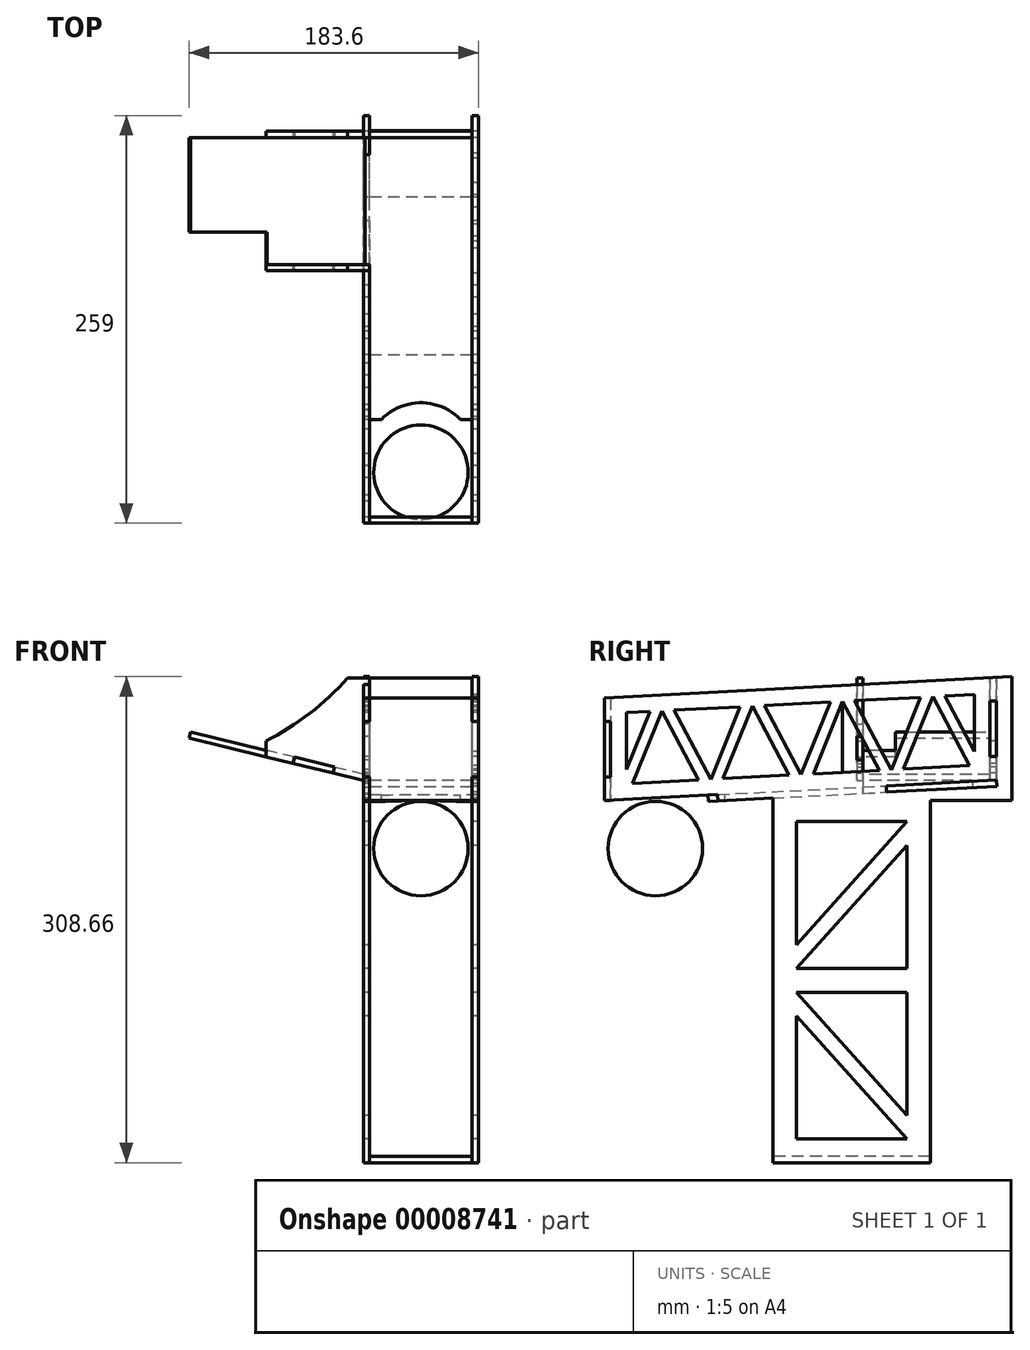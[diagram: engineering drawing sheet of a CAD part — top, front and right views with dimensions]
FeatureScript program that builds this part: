
annotation { "Feature Type Name" : "Feature", "Feature Type Description" : "" }
export const myFeature = defineFeature(function(context is Context, id is Id, definition is map)
    precondition{}
    {
        {
            var Q0;
            Q0=qCreatedBy(makeId("Right.planeOp"),FACE);
            var sketch = newSketch(context, id + "F0", { "sketchPlane" : qUnion([Q0])});
            skLineSegment(sketch, "E0", {"start": v(0, 0) * mm, "end": v(71.9, 3.77) * mm});
            skLineSegment(sketch, "E1", {"start": v(249, 78.14) * mm, "end": v(0, 65.09) * mm});
            skLineSegment(sketch, "E2", {"start": v(0, 65.09) * mm, "end": v(0, 50.09) * mm});
            skLineSegment(sketch, "E3.top", {"start": v(71.9, 0) * mm, "end": v(0, 0) * mm, "construction": true});
            skPoint(sketch, "E4.orphan", {"position": v(249, 13.05) * mm});
            skLineSegment(sketch, "E5", {"start": v(249, 13.05) * mm, "end": v(249.2, 9.06) * mm, "construction": true});
            skLineSegment(sketch, "E6", {"start": v(249, 78.14) * mm, "end": v(249, 13.05) * mm, "construction": true});
            skLineSegment(sketch, "E7", {"start": v(249.2, 9.06) * mm, "end": v(249, 13.05) * mm});
            skLineSegment(sketch, "E8", {"start": v(179.1, 9.39) * mm, "end": v(179.3, 5.4) * mm});
            skLineSegment(sketch, "E9", {"start": v(179.3, 5.4) * mm, "end": v(249.2, 9.06) * mm});
            skLineSegment(sketch, "E10.bottom", {"start": v(249, 63.14) * mm, "end": v(245, 63.14) * mm});
            skLineSegment(sketch, "E10.top", {"start": v(249, 28.14) * mm, "end": v(245, 28.14) * mm});
            skLineSegment(sketch, "E10.left", {"start": v(249, 63.14) * mm, "end": v(249, 28.14) * mm});
            skLineSegment(sketch, "E10.right", {"start": v(245, 63.14) * mm, "end": v(245, 28.14) * mm});
            skLineSegment(sketch, "E11", {"start": v(179.1, 9.39) * mm, "end": v(249, 13.05) * mm});
            skLineSegment(sketch, "E12", {"start": v(72.11, -0.23) * mm, "end": v(107.06, 1.6) * mm});
            skLineSegment(sketch, "E13", {"start": v(71.9, 3.77) * mm, "end": v(72.11, -0.23) * mm});
            skLineSegment(sketch, "E14.bottom", {"start": v(0, 50.09) * mm, "end": v(4, 50.09) * mm});
            skLineSegment(sketch, "E14.top", {"start": v(0, 15.09) * mm, "end": v(4, 15.09) * mm});
            skLineSegment(sketch, "E14.right", {"start": v(4, 50.09) * mm, "end": v(4, 15.09) * mm});
            skLineSegment(sketch, "E15.trimOffspring", {"start": v(0, 15.09) * mm, "end": v(0, 0) * mm});
            skLineSegment(sketch, "E16", {"start": v(14, 55.8) * mm, "end": v(28.9, 56.59) * mm});
            skLineSegment(sketch, "E17", {"start": v(235, 67.4) * mm, "end": v(235, 31.3) * mm});
            skLineSegment(sketch, "E18", {"start": v(231.93, 22.17) * mm, "end": v(190.02, 19.97) * mm});
            skLineSegment(sketch, "E19", {"start": v(14, 19.72) * mm, "end": v(14, 55.8) * mm});
            skLineSegment(sketch, "E20", {"start": v(44.32, 57.4) * mm, "end": v(67.63, 13.56) * mm});
            skLineSegment(sketch, "E21", {"start": v(75.35, 13.96) * mm, "end": v(93.95, 60) * mm});
            skLineSegment(sketch, "E22", {"start": v(101.66, 60.4) * mm, "end": v(124.97, 16.56) * mm});
            skLineSegment(sketch, "E23", {"start": v(132.68, 16.97) * mm, "end": v(151.28, 63) * mm});
            skLineSegment(sketch, "E24", {"start": v(159, 63.4) * mm, "end": v(182.3, 19.57) * mm});
            skLineSegment(sketch, "E25", {"start": v(36.6, 57) * mm, "end": v(59.92, 13.15) * mm});
            skLineSegment(sketch, "E26", {"start": v(67.63, 13.56) * mm, "end": v(86.23, 59.6) * mm});
            skLineSegment(sketch, "E27", {"start": v(93.95, 60) * mm, "end": v(117.26, 16.16) * mm});
            skLineSegment(sketch, "E28", {"start": v(124.97, 16.56) * mm, "end": v(143.57, 62.6) * mm});
            skLineSegment(sketch, "E29", {"start": v(151.28, 63) * mm, "end": v(174.6, 19.16) * mm});
            skLineSegment(sketch, "E30", {"start": v(182.3, 19.57) * mm, "end": v(200.9, 65.6) * mm});
            skLineSegment(sketch, "E31", {"start": v(190.02, 19.97) * mm, "end": v(208.62, 66) * mm});
            skLineSegment(sketch, "E32", {"start": v(208.62, 66) * mm, "end": v(231.93, 22.17) * mm});
            skLineSegment(sketch, "E33", {"start": v(216.33, 66.41) * mm, "end": v(235, 31.3) * mm});
            skLineSegment(sketch, "E34", {"start": v(36.6, 57) * mm, "end": v(18, 10.96) * mm});
            skLineSegment(sketch, "E35", {"start": v(28.9, 56.59) * mm, "end": v(14, 19.72) * mm});
            skLineSegment(sketch, "E36.trimOffspring", {"start": v(44.32, 57.4) * mm, "end": v(86.23, 59.6) * mm});
            skLineSegment(sketch, "E37.trimOffspring", {"start": v(59.92, 13.15) * mm, "end": v(18, 10.96) * mm});
            skLineSegment(sketch, "E38.trimOffspring", {"start": v(101.66, 60.4) * mm, "end": v(143.57, 62.6) * mm});
            skLineSegment(sketch, "E39.trimOffspring", {"start": v(159, 63.4) * mm, "end": v(200.9, 65.6) * mm});
            skLineSegment(sketch, "E40.trimOffspring", {"start": v(117.26, 16.16) * mm, "end": v(75.35, 13.96) * mm});
            skLineSegment(sketch, "E41.trimOffspring", {"start": v(216.33, 66.41) * mm, "end": v(235, 67.4) * mm});
            skLineSegment(sketch, "E42", {"start": v(132.68, 16.97) * mm, "end": v(174.6, 19.16) * mm});
            skLineSegment(sketch, "E43", {"start": v(107.06, 1.6) * mm, "end": v(107.06, -230) * mm});
            skLineSegment(sketch, "E44", {"start": v(107.06, -230) * mm, "end": v(207.06, -230) * mm});
            skLineSegment(sketch, "E45", {"start": v(259, 0) * mm, "end": v(259, 78.66) * mm});
            skLineSegment(sketch, "E46", {"start": v(259, 78.66) * mm, "end": v(249, 78.14) * mm});
            skLineSegment(sketch, "E47", {"start": v(259, 0) * mm, "end": v(207.06, 0) * mm});
            skLineSegment(sketch, "E48", {"start": v(207.06, 0) * mm, "end": v(207.06, -230) * mm});
            skLineSegment(sketch, "E49", {"start": v(122.06, -13.4) * mm, "end": v(192.06, -13.4) * mm});
            skLineSegment(sketch, "E50", {"start": v(192.06, -13.4) * mm, "end": v(122.06, -91.7) * mm});
            skLineSegment(sketch, "E51", {"start": v(122.06, -91.7) * mm, "end": v(122.06, -13.4) * mm});
            skLineSegment(sketch, "E52", {"start": v(122.06, -106.7) * mm, "end": v(192.06, -28.4) * mm});
            skLineSegment(sketch, "E53", {"start": v(192.06, -28.4) * mm, "end": v(192.06, -106.7) * mm});
            skLineSegment(sketch, "E54", {"start": v(192.06, -106.7) * mm, "end": v(122.06, -106.7) * mm});
            skLineSegment(sketch, "E55", {"start": v(122.06, -121.7) * mm, "end": v(192.06, -200) * mm});
            skLineSegment(sketch, "E56", {"start": v(192.06, -200) * mm, "end": v(192.06, -121.7) * mm});
            skLineSegment(sketch, "E57", {"start": v(192.06, -121.7) * mm, "end": v(122.06, -121.7) * mm});
            skLineSegment(sketch, "E58", {"start": v(122.06, -136.7) * mm, "end": v(192.06, -215) * mm});
            skLineSegment(sketch, "E59", {"start": v(192.06, -215) * mm, "end": v(122.06, -215) * mm});
            skLineSegment(sketch, "E60", {"start": v(122.06, -215) * mm, "end": v(122.06, -136.7) * mm});
            skSolve(sketch);
        }
        {
            var Q0;
            Q0 = qSketchRegion(id + "F0", true);
            extrude(context, id + "F1", {"entities" : qUnion([Q0]), "depth" : 4 * mm});
        }
        {
            var Q0;
            Q0=makeQuery(id+"F1.opExtrude","SWEPT_FACE",FACE,{"disambiguationData":[OSD([sQuery(id+"F0.wireOp",EDGE,"E0")])]});
            var sketch = newSketch(context, id + "F2", { "sketchPlane" : qUnion([Q0])});
            skLineSegment(sketch, "E61.top", {"start": v(4, -249.34) * mm, "end": v(0, -249.34) * mm});
            skLineSegment(sketch, "E61.left", {"start": v(4, -66) * mm, "end": v(4, -72) * mm});
            skLineSegment(sketch, "E61.right", {"start": v(-69, -66) * mm, "end": v(-69, -72) * mm});
            skLineSegment(sketch, "E62", {"start": v(4, -66) * mm, "end": v(-7.36, -66) * mm});
            skLineSegment(sketch, "E63", {"start": v(-65, -249.34) * mm, "end": v(0, -249.34) * mm});
            skLineSegment(sketch, "E64", {"start": v(0, -72) * mm, "end": v(0, -179.34) * mm});
            skLineSegment(sketch, "E65.0", {"start": v(4, -72) * mm, "end": v(0, -72) * mm});
            skLineSegment(sketch, "E66.0", {"start": v(4, -179.34) * mm, "end": v(0, -179.34) * mm});
            skLineSegment(sketch, "E67", {"start": v(4, -179.34) * mm, "end": v(4, -249.34) * mm});
            skLineSegment(sketch, "E68", {"start": v(0, -249.34) * mm, "end": v(4, -249.34) * mm});
            skLineSegment(sketch, "E69.trimOffspring", {"start": v(0, -66) * mm, "end": v(0, 0) * mm});
            skLineSegment(sketch, "E70.bottom", {"start": v(-69, -234.34) * mm, "end": v(-65, -234.34) * mm});
            skLineSegment(sketch, "E70.top", {"start": v(-69, -164.34) * mm, "end": v(-65, -164.34) * mm});
            skLineSegment(sketch, "E71", {"start": v(-65, -234.34) * mm, "end": v(-65, -249.34) * mm});
            skLineSegment(sketch, "E72", {"start": v(-69, -72) * mm, "end": v(-65, -72) * mm});
            skLineSegment(sketch, "E73", {"start": v(-65, -72) * mm, "end": v(-65, -164.34) * mm});
            skLineSegment(sketch, "E74.trimOffspring", {"start": v(-69, -164.34) * mm, "end": v(-69, -234.34) * mm});
            skArc(sketch, "E75", {"start": v(-57.64, -66) * mm, "mid": v(-32.5, -76.65) * mm, "end": v(-7.36, -66) * mm});
            skLineSegment(sketch, "E76", {"start": v(-32.5, -66) * mm, "end": v(-32.5, -249.34) * mm, "construction": true});
            skLineSegment(sketch, "E77.trimOffspring", {"start": v(-57.64, -66) * mm, "end": v(-69, -66) * mm});
            skSolve(sketch);
        }
        {
            var Q0;
            Q0 = qSketchRegion(id + "F2", true);
            extrude(context, id + "F3", {"entities" : qUnion([Q0]), "depth" : 4 * mm});
        }
        {
            var Q0;
            Q0=makeQuery(id+"F3.opExtrude","SWEPT_FACE",FACE,{"disambiguationData":[OSD([sQuery(id+"F2.wireOp",EDGE,"E61.right")])]});
            var sketch = newSketch(context, id + "F4", { "sketchPlane" : qUnion([Q0])});
            skPoint(sketch, "E78.0.2.start.orphan", {"position": v(0, 65.09) * mm});
            skLineSegment(sketch, "E79.1", {"start": v(-249, 63.14) * mm, "end": v(-249, 28.14) * mm});
            skLineSegment(sketch, "E79.2", {"start": v(-249, 63.14) * mm, "end": v(-245, 63.14) * mm});
            skLineSegment(sketch, "E79.4", {"start": v(-249, 28.14) * mm, "end": v(-245, 28.14) * mm});
            skLineSegment(sketch, "E79.11", {"start": v(-164.33, 4.6) * mm, "end": v(-234.23, 8.27) * mm});
            skLineSegment(sketch, "E79.12", {"start": v(-234.23, 8.27) * mm, "end": v(-234.02, 12.26) * mm});
            skLineSegment(sketch, "E79.14", {"start": v(-164.33, 8.61) * mm, "end": v(-164.33, 4.6) * mm});
            skLineSegment(sketch, "E79.26", {"start": v(-72.11, -0.23) * mm, "end": v(-107.06, 1.6) * mm});
            skLineSegment(sketch, "E79.27", {"start": v(-71.9, 3.77) * mm, "end": v(-72.11, -0.23) * mm});
            skLineSegment(sketch, "E79.28", {"start": v(0, 0) * mm, "end": v(-71.9, 3.77) * mm});
            skLineSegment(sketch, "E79.29", {"start": v(0, 65.09) * mm, "end": v(0, 50.09) * mm});
            skLineSegment(sketch, "E80", {"start": v(-245, 63.14) * mm, "end": v(-245, 77.93) * mm});
            skLineSegment(sketch, "E81", {"start": v(-245, 28.14) * mm, "end": v(-245, 12.84) * mm});
            skLineSegment(sketch, "E82", {"start": v(-245, 12.84) * mm, "end": v(-234.02, 12.26) * mm});
            skLineSegment(sketch, "E83", {"start": v(-164.33, 73.7) * mm, "end": v(-164.33, 63.7) * mm});
            skLineSegment(sketch, "E84", {"start": v(0, 50.09) * mm, "end": v(-4, 50.09) * mm});
            skLineSegment(sketch, "E85", {"start": v(-4, 50.09) * mm, "end": v(-4, 15.09) * mm});
            skLineSegment(sketch, "E86", {"start": v(-4, 15.09) * mm, "end": v(0, 15.09) * mm});
            skLineSegment(sketch, "E87.trimOffspring", {"start": v(0, 15.09) * mm, "end": v(0, 0) * mm});
            skLineSegment(sketch, "E88.trimOffspring", {"start": v(0, 50.09) * mm, "end": v(0, 65.09) * mm});
            skPoint(sketch, "E78.0.0.start.orphan", {"position": v(0, 50.09) * mm});
            skLineSegment(sketch, "E89.0", {"start": v(-124.97, 16.56) * mm, "end": v(-143.57, 62.6) * mm});
            skLineSegment(sketch, "E89.1", {"start": v(-101.66, 60.4) * mm, "end": v(-143.57, 62.6) * mm});
            skLineSegment(sketch, "E89.2", {"start": v(-101.66, 60.4) * mm, "end": v(-124.97, 16.56) * mm});
            skLineSegment(sketch, "E89.3", {"start": v(-75.35, 13.96) * mm, "end": v(-93.95, 60) * mm});
            skLineSegment(sketch, "E89.4", {"start": v(-93.95, 60) * mm, "end": v(-117.26, 16.16) * mm});
            skLineSegment(sketch, "E89.5", {"start": v(-44.32, 57.4) * mm, "end": v(-86.23, 59.6) * mm});
            skLineSegment(sketch, "E89.6", {"start": v(-67.63, 13.56) * mm, "end": v(-86.23, 59.6) * mm});
            skLineSegment(sketch, "E89.7", {"start": v(-44.32, 57.4) * mm, "end": v(-67.63, 13.56) * mm});
            skLineSegment(sketch, "E89.8", {"start": v(-36.6, 57) * mm, "end": v(-18, 10.96) * mm});
            skLineSegment(sketch, "E89.9", {"start": v(-36.6, 57) * mm, "end": v(-59.92, 13.15) * mm});
            skLineSegment(sketch, "E89.10", {"start": v(-14, 55.8) * mm, "end": v(-28.9, 56.59) * mm});
            skLineSegment(sketch, "E89.11", {"start": v(-28.9, 56.59) * mm, "end": v(-14, 19.72) * mm});
            skLineSegment(sketch, "E89.12", {"start": v(-14, 19.72) * mm, "end": v(-14, 55.8) * mm});
            skLineSegment(sketch, "E89.13", {"start": v(-59.92, 13.15) * mm, "end": v(-18, 10.96) * mm});
            skLineSegment(sketch, "E89.14", {"start": v(-117.26, 16.16) * mm, "end": v(-75.35, 13.96) * mm});
            skLineSegment(sketch, "E89.15", {"start": v(-132.68, 16.97) * mm, "end": v(-151.28, 17.94) * mm});
            skLineSegment(sketch, "E89.16", {"start": v(-132.68, 16.97) * mm, "end": v(-151.28, 63) * mm});
            skPoint(sketch, "E90.orphan", {"position": v(-174.6, 19.16) * mm});
            skLineSegment(sketch, "E91", {"start": v(-164.33, 63.7) * mm, "end": v(-160.33, 63.7) * mm});
            skLineSegment(sketch, "E92", {"start": v(-160.33, 63.7) * mm, "end": v(-160.33, 48.7) * mm});
            skLineSegment(sketch, "E93", {"start": v(-160.33, 48.7) * mm, "end": v(-164.33, 48.7) * mm});
            skLineSegment(sketch, "E94", {"start": v(-164.33, 40.7) * mm, "end": v(-160.33, 40.7) * mm});
            skLineSegment(sketch, "E95", {"start": v(-160.33, 40.7) * mm, "end": v(-160.33, 25.7) * mm});
            skLineSegment(sketch, "E96", {"start": v(-160.33, 25.7) * mm, "end": v(-164.33, 25.7) * mm});
            skLineSegment(sketch, "E97.trimOffspring", {"start": v(-164.33, 48.7) * mm, "end": v(-164.33, 40.7) * mm});
            skLineSegment(sketch, "E98.trimOffspring", {"start": v(-164.33, 25.7) * mm, "end": v(-164.33, 8.61) * mm});
            skLineSegment(sketch, "E99", {"start": v(-107.06, 1.6) * mm, "end": v(-107.06, -230) * mm});
            skLineSegment(sketch, "E100", {"start": v(-107.06, -230) * mm, "end": v(-207.06, -230) * mm});
            skLineSegment(sketch, "E101", {"start": v(-259, 0) * mm, "end": v(-259, 78.66) * mm});
            skLineSegment(sketch, "E102", {"start": v(-245, 77.93) * mm, "end": v(-259, 78.66) * mm});
            skLineSegment(sketch, "E103", {"start": v(0, 65.09) * mm, "end": v(-164.33, 73.7) * mm});
            skLineSegment(sketch, "E104", {"start": v(-151.28, 17.94) * mm, "end": v(-151.28, 63) * mm});
            skLineSegment(sketch, "E105", {"start": v(-207.06, -230) * mm, "end": v(-207.06, 0) * mm});
            skLineSegment(sketch, "E106", {"start": v(-207.06, 0) * mm, "end": v(-259, 0) * mm});
            skLineSegment(sketch, "E107.0", {"start": v(-122.06, -13.4) * mm, "end": v(-192.06, -13.4) * mm});
            skLineSegment(sketch, "E108.0", {"start": v(-122.06, -91.7) * mm, "end": v(-122.06, -13.4) * mm});
            skLineSegment(sketch, "E109.0", {"start": v(-192.06, -13.4) * mm, "end": v(-122.06, -91.7) * mm});
            skLineSegment(sketch, "E110.0", {"start": v(-122.06, -106.7) * mm, "end": v(-192.06, -28.4) * mm});
            skLineSegment(sketch, "E111.0", {"start": v(-192.06, -28.4) * mm, "end": v(-192.06, -106.7) * mm});
            skLineSegment(sketch, "E112.0", {"start": v(-192.06, -106.7) * mm, "end": v(-122.06, -106.7) * mm});
            skLineSegment(sketch, "E113.0", {"start": v(-192.06, -121.7) * mm, "end": v(-122.06, -121.7) * mm});
            skLineSegment(sketch, "E114.0", {"start": v(-192.06, -200) * mm, "end": v(-192.06, -121.7) * mm});
            skLineSegment(sketch, "E115.0", {"start": v(-122.06, -121.7) * mm, "end": v(-192.06, -200) * mm});
            skLineSegment(sketch, "E116.0", {"start": v(-122.06, -136.7) * mm, "end": v(-192.06, -215) * mm});
            skLineSegment(sketch, "E117.0", {"start": v(-122.06, -215) * mm, "end": v(-122.06, -136.7) * mm});
            skLineSegment(sketch, "E118.0", {"start": v(-192.06, -215) * mm, "end": v(-122.06, -215) * mm});
            skSolve(sketch);
        }
        {
            var Q0;
            Q0 = qSketchRegion(id + "F4", true);
            extrude(context, id + "F5", {"entities" : qUnion([Q0]), "oppositeDirection" : true, "depth" : 4 * mm});
        }
        {
            var Q0;
            Q0=makeQuery(id+"F5.opExtrude","SWEPT_FACE",FACE,{"disambiguationData":[OSD([sQuery(id+"F4.wireOp",EDGE,"E85")])]});
            var sketch = newSketch(context, id + "F6", { "sketchPlane" : qUnion([Q0])});
            skLineSegment(sketch, "E119", {"start": v(-65, 65.09) * mm, "end": v(0, 65.09) * mm});
            skLineSegment(sketch, "E120", {"start": v(0, 65.09) * mm, "end": v(0, 50.09) * mm});
            skLineSegment(sketch, "E121", {"start": v(0, 50.09) * mm, "end": v(4, 50.09) * mm});
            skLineSegment(sketch, "E122", {"start": v(4, 50.09) * mm, "end": v(4, 15.09) * mm});
            skLineSegment(sketch, "E123", {"start": v(4, 15.09) * mm, "end": v(0, 15.09) * mm});
            skLineSegment(sketch, "E124", {"start": v(0, 15.09) * mm, "end": v(0, 0) * mm});
            skLineSegment(sketch, "E125", {"start": v(0, 0) * mm, "end": v(-65, 0) * mm});
            skLineSegment(sketch, "E126", {"start": v(-65, 0) * mm, "end": v(-65, 15.09) * mm});
            skLineSegment(sketch, "E127", {"start": v(-65, 15.09) * mm, "end": v(-69, 15.09) * mm});
            skLineSegment(sketch, "E128", {"start": v(-69, 15.09) * mm, "end": v(-69, 50.09) * mm});
            skLineSegment(sketch, "E129", {"start": v(-69, 50.09) * mm, "end": v(-65, 50.09) * mm});
            skLineSegment(sketch, "E130", {"start": v(-65, 50.09) * mm, "end": v(-65, 65.09) * mm});
            skSolve(sketch);
        }
        {
            var Q0;
            Q0 = qSketchRegion(id + "F6", true);
            extrude(context, id + "F7", {"entities" : qUnion([Q0]), "depth" : 4 * mm});
        }
        {
            var Q0;
            Q0=makeQuery(id+"F1.opExtrude","SWEPT_FACE",FACE,{"disambiguationData":[OSD([sQuery(id+"F0.wireOp",EDGE,"E10.right")])]});
            var sketch = newSketch(context, id + "F8", { "sketchPlane" : qUnion([Q0])});
            skLineSegment(sketch, "E131", {"start": v(65, 63.14) * mm, "end": v(65, 63.14) * mm});
            skLineSegment(sketch, "E132", {"start": v(65, 63.14) * mm, "end": v(69, 63.14) * mm});
            skLineSegment(sketch, "E133", {"start": v(69, 63.14) * mm, "end": v(69, 63.14) * mm});
            skLineSegment(sketch, "E134", {"start": v(131, 37.84) * mm, "end": v(131, 27.84) * mm});
            skLineSegment(sketch, "E135", {"start": v(131, 27.84) * mm, "end": v(113.71, 23.66) * mm});
            skLineSegment(sketch, "E136", {"start": v(69, 12.84) * mm, "end": v(69, 28.14) * mm});
            skLineSegment(sketch, "E137", {"start": v(69, 28.14) * mm, "end": v(65, 28.14) * mm});
            skLineSegment(sketch, "E138", {"start": v(65, 28.14) * mm, "end": v(65, 13.05) * mm});
            skLineSegment(sketch, "E139", {"start": v(65, 13.05) * mm, "end": v(0, 13.05) * mm});
            skLineSegment(sketch, "E140", {"start": v(0, 13.05) * mm, "end": v(0, 28.14) * mm});
            skLineSegment(sketch, "E141", {"start": v(0, 28.14) * mm, "end": v(-4, 28.14) * mm});
            skLineSegment(sketch, "E142", {"start": v(-4, 28.14) * mm, "end": v(-4, 63.14) * mm});
            skLineSegment(sketch, "E143", {"start": v(-4, 63.14) * mm, "end": v(0, 63.14) * mm});
            skLineSegment(sketch, "E144", {"start": v(0, 63.14) * mm, "end": v(0, 63.14) * mm});
            skLineSegment(sketch, "E145", {"start": v(69, 12.84) * mm, "end": v(131, 12.84) * mm, "construction": true});
            skLineSegment(sketch, "E146", {"start": v(131, 12.84) * mm, "end": v(131, 27.84) * mm, "construction": true});
            skArc(sketch, "E147", {"start": v(79, 77.93) * mm, "mid": v(103.1, 55.42) * mm, "end": v(131, 37.84) * mm});
            skLineSegment(sketch, "E148", {"start": v(88.44, 17.54) * mm, "end": v(87.5, 21.43) * mm});
            skLineSegment(sketch, "E149", {"start": v(87.5, 21.43) * mm, "end": v(112.77, 27.54) * mm});
            skLineSegment(sketch, "E150", {"start": v(112.77, 27.54) * mm, "end": v(113.71, 23.66) * mm});
            skLineSegment(sketch, "E151.trimOffspring", {"start": v(88.44, 17.54) * mm, "end": v(69, 12.84) * mm});
            skLineSegment(sketch, "E152", {"start": v(0, 63.14) * mm, "end": v(0, 77.93) * mm});
            skLineSegment(sketch, "E153", {"start": v(0, 77.93) * mm, "end": v(65, 77.93) * mm});
            skLineSegment(sketch, "E154", {"start": v(65, 77.93) * mm, "end": v(65, 63.14) * mm});
            skLineSegment(sketch, "E155", {"start": v(69, 63.14) * mm, "end": v(69, 77.93) * mm});
            skLineSegment(sketch, "E156", {"start": v(69, 77.93) * mm, "end": v(79, 77.93) * mm});
            skSolve(sketch);
        }
        {
            var Q0;
            Q0 = qSketchRegion(id + "F8", true);
            extrude(context, id + "F9", {"entities" : qUnion([Q0]), "depth" : 4 * mm});
        }
        {
            var Q0;
            Q0=makeQuery(id+"F9.opExtrude","SWEPT_FACE",FACE,{"disambiguationData":[OSD([sQuery(id+"F8.wireOp",EDGE,"E135")])]});
            var sketch = newSketch(context, id + "F10", { "sketchPlane" : qUnion([Q0])});
            skLineSegment(sketch, "E157.top", {"start": v(-70.08, -164.33) * mm, "end": v(-90.08, -164.33) * mm});
            skLineSegment(sketch, "E157.right", {"start": v(-133.87, -185) * mm, "end": v(-133.87, -164.33) * mm});
            skLineSegment(sketch, "E158.bottom", {"start": v(-133.87, -185) * mm, "end": v(-183.87, -185) * mm});
            skLineSegment(sketch, "E158.top", {"start": v(-133.87, -245) * mm, "end": v(-183.87, -245) * mm});
            skLineSegment(sketch, "E158.right", {"start": v(-183.87, -185) * mm, "end": v(-183.87, -245) * mm});
            skLineSegment(sketch, "E159", {"start": v(-116.08, -245) * mm, "end": v(-116.08, -249) * mm});
            skLineSegment(sketch, "E160", {"start": v(-116.08, -249) * mm, "end": v(-90.08, -249) * mm});
            skLineSegment(sketch, "E161", {"start": v(-90.08, -249) * mm, "end": v(-90.08, -245) * mm});
            skLineSegment(sketch, "E162", {"start": v(-116.08, -164.33) * mm, "end": v(-116.08, -160.33) * mm});
            skLineSegment(sketch, "E163", {"start": v(-116.08, -160.33) * mm, "end": v(-90.08, -160.33) * mm});
            skLineSegment(sketch, "E164", {"start": v(-90.08, -160.33) * mm, "end": v(-90.08, -164.33) * mm});
            skLineSegment(sketch, "E165.trimOffspring", {"start": v(-116.08, -245) * mm, "end": v(-133.87, -245) * mm});
            skLineSegment(sketch, "E166.trimOffspring", {"start": v(-116.08, -164.33) * mm, "end": v(-133.87, -164.33) * mm});
            skLineSegment(sketch, "E167", {"start": v(-70.08, -244.84) * mm, "end": v(-70.08, -164.33) * mm});
            skLineSegment(sketch, "E168", {"start": v(-90.08, -245) * mm, "end": v(-70.08, -244.84) * mm});
            skSolve(sketch);
        }
        {
            var Q0;
            Q0 = qSketchRegion(id + "F10", true);
            extrude(context, id + "F11", {"entities" : qUnion([Q0]), "oppositeDirection" : true, "depth" : 4 * mm});
        }
        {
            var Q0;
            Q0=makeQuery(id+"F11.opExtrude","SWEPT_FACE",FACE,{"disambiguationData":[OSD([sQuery(id+"F10.wireOp",EDGE,"E157.top")])]});
            var sketch = newSketch(context, id + "F12", { "sketchPlane" : qUnion([Q0])});
            skLineSegment(sketch, "E169.1", {"start": v(-69, 12.84) * mm, "end": v(-69, 12.84) * mm});
            skLineSegment(sketch, "E170", {"start": v(-69, 12.84) * mm, "end": v(-88.44, 17.54) * mm});
            skLineSegment(sketch, "E171.0", {"start": v(-131, 37.84) * mm, "end": v(-131, 27.84) * mm});
            skArc(sketch, "E171.1", {"start": v(-131, 37.84) * mm, "mid": v(-288.9, 350.2) * mm, "end": v(-131, 37.84) * mm});
            skLineSegment(sketch, "E172", {"start": v(-112.77, 27.54) * mm, "end": v(-113.71, 23.66) * mm});
            skLineSegment(sketch, "E173", {"start": v(-112.77, 27.54) * mm, "end": v(-87.5, 21.43) * mm});
            skLineSegment(sketch, "E174", {"start": v(-87.5, 21.43) * mm, "end": v(-88.44, 17.54) * mm});
            skLineSegment(sketch, "E175.trimOffspring", {"start": v(-113.71, 23.66) * mm, "end": v(-131, 27.84) * mm});
            skLineSegment(sketch, "E176.3", {"start": v(-65, 48.7) * mm, "end": v(-69, 48.7) * mm});
            skLineSegment(sketch, "E176.4", {"start": v(-69, 48.7) * mm, "end": v(-69, 40.7) * mm});
            skLineSegment(sketch, "E176.5", {"start": v(-65, 40.7) * mm, "end": v(-69, 40.7) * mm});
            skLineSegment(sketch, "E176.6", {"start": v(-65, 25.7) * mm, "end": v(-69, 25.7) * mm});
            skLineSegment(sketch, "E176.7", {"start": v(-69, 25.7) * mm, "end": v(-69, 12.84) * mm});
            skLineSegment(sketch, "E177.trimOffspring", {"start": v(-65, 63.7) * mm, "end": v(-65, 48.7) * mm});
            skLineSegment(sketch, "E178.trimOffspring", {"start": v(-65, 40.7) * mm, "end": v(-65, 25.7) * mm});
            skPoint(sketch, "E179.orphan", {"position": v(-69, 25.7) * mm});
            skLineSegment(sketch, "E180.0", {"start": v(-65, 63.7) * mm, "end": v(-69, 63.7) * mm});
            skLineSegment(sketch, "E180.1", {"start": v(-69, 73.7) * mm, "end": v(-69, 63.7) * mm});
            skLineSegment(sketch, "E181.0", {"start": v(-65, 77.93) * mm, "end": v(-79, 77.93) * mm});
            skArc(sketch, "E181.1", {"start": v(-79, 77.93) * mm, "mid": v(-103.1, 55.42) * mm, "end": v(-131, 37.84) * mm});
            skLineSegment(sketch, "E182.0", {"start": v(-65, 73.7) * mm, "end": v(-69, 73.7) * mm});
            skLineSegment(sketch, "E183", {"start": v(-65, 73.7) * mm, "end": v(-65, 77.93) * mm});
            skSolve(sketch);
        }
        {
            var Q0;
            Q0 = qSketchRegion(id + "F12", true);
            extrude(context, id + "F13", {"entities" : qUnion([Q0]), "depth" : 4 * mm});
        }
        {
            var Q0;
            Q0=makeQuery(id+"F5.opExtrude","CAP_FACE",FACE,{"disambiguationData":[OSD([sQuery(id+"F4.wireOp",EDGE,"E78.0.1"),sQuery(id+"F4.wireOp",EDGE,"E79.0"),sQuery(id+"F4.wireOp",EDGE,"E79.1"),sQuery(id+"F4.wireOp",EDGE,"E79.2"),sQuery(id+"F4.wireOp",EDGE,"E79.4"),sQuery(id+"F4.wireOp",EDGE,"E79.5"),sQuery(id+"F4.wireOp",EDGE,"E79.6"),sQuery(id+"F4.wireOp",EDGE,"E79.7"),sQuery(id+"F4.wireOp",EDGE,"E79.8"),sQuery(id+"F4.wireOp",EDGE,"E79.9"),sQuery(id+"F4.wireOp",EDGE,"E79.10"),sQuery(id+"F4.wireOp",EDGE,"E79.11"),sQuery(id+"F4.wireOp",EDGE,"E79.12"),sQuery(id+"F4.wireOp",EDGE,"E79.14"),sQuery(id+"F4.wireOp",EDGE,"E79.15"),sQuery(id+"F4.wireOp",EDGE,"E79.16"),sQuery(id+"F4.wireOp",EDGE,"E79.17"),sQuery(id+"F4.wireOp",EDGE,"E79.18"),sQuery(id+"F4.wireOp",EDGE,"E79.19"),sQuery(id+"F4.wireOp",EDGE,"E79.20"),sQuery(id+"F4.wireOp",EDGE,"E79.21"),sQuery(id+"F4.wireOp",EDGE,"E79.22"),sQuery(id+"F4.wireOp",EDGE,"E79.23"),sQuery(id+"F4.wireOp",EDGE,"E79.24"),sQuery(id+"F4.wireOp",EDGE,"E79.25"),sQuery(id+"F4.wireOp",EDGE,"E79.26"),sQuery(id+"F4.wireOp",EDGE,"E79.27"),sQuery(id+"F4.wireOp",EDGE,"E79.28"),sQuery(id+"F4.wireOp",EDGE,"E80"),sQuery(id+"F4.wireOp",EDGE,"4ae15630-7873-4519-9142-a34cefbef92f"),sQuery(id+"F4.wireOp",EDGE,"E81"),sQuery(id+"F4.wireOp",EDGE,"E82"),sQuery(id+"F4.wireOp",EDGE,"E83"),sQuery(id+"F4.wireOp",EDGE,"ef37c952-c681-47c9-a026-029117f68ef9"),sQuery(id+"F4.wireOp",EDGE,"E84"),sQuery(id+"F4.wireOp",EDGE,"E85"),sQuery(id+"F4.wireOp",EDGE,"E86"),sQuery(id+"F4.wireOp",EDGE,"E87.trimOffspring"),sQuery(id+"F4.wireOp",EDGE,"E88.trimOffspring"),sQuery(id+"F4.wireOp",EDGE,"E89.0"),sQuery(id+"F4.wireOp",EDGE,"E89.1"),sQuery(id+"F4.wireOp",EDGE,"E89.2"),sQuery(id+"F4.wireOp",EDGE,"E89.3"),sQuery(id+"F4.wireOp",EDGE,"E89.4"),sQuery(id+"F4.wireOp",EDGE,"E89.5"),sQuery(id+"F4.wireOp",EDGE,"E89.6"),sQuery(id+"F4.wireOp",EDGE,"E89.7"),sQuery(id+"F4.wireOp",EDGE,"E89.8"),sQuery(id+"F4.wireOp",EDGE,"E89.9"),sQuery(id+"F4.wireOp",EDGE,"E89.10"),sQuery(id+"F4.wireOp",EDGE,"E89.11"),sQuery(id+"F4.wireOp",EDGE,"E89.12"),sQuery(id+"F4.wireOp",EDGE,"E89.13"),sQuery(id+"F4.wireOp",EDGE,"E89.14"),sQuery(id+"F4.wireOp",EDGE,"E89.15"),sQuery(id+"F4.wireOp",EDGE,"E89.16"),sQuery(id+"F4.wireOp",EDGE,"E89.17"),sQuery(id+"F4.wireOp",EDGE,"e613d2b2-fb36-4108-9489-dbbc835d8e5d")])],"isStart":true});
            var Q1;
            Q1=makeQuery(id+"F1.opExtrude","CAP_FACE",FACE,{"disambiguationData":[OSD([sQuery(id+"F0.wireOp",EDGE,"E0"),sQuery(id+"F0.wireOp",EDGE,"E1"),sQuery(id+"F0.wireOp",EDGE,"E2"),sQuery(id+"F0.wireOp",EDGE,"ecbc3025-46a1-4a21-8c2d-8ca136fd10ce"),sQuery(id+"F0.wireOp",EDGE,"2880ab20-c187-474d-a706-7b57105d8e94"),sQuery(id+"F0.wireOp",EDGE,"0fddf1f1-f98e-4ab2-9615-00887aecef17"),sQuery(id+"F0.wireOp",EDGE,"208d794d-60aa-41b5-82c0-fe83a0807e02"),sQuery(id+"F0.wireOp",EDGE,"ad43ec8c-1358-4201-866b-06ab896043ed.trimOffspring"),sQuery(id+"F0.wireOp",EDGE,"6aec1979-b0b5-4794-90ce-a0e7edb21cd4.trimOffspring"),sQuery(id+"F0.wireOp",EDGE,"781f0303-0491-42ec-a057-bea1d53d88dd"),sQuery(id+"F0.wireOp",EDGE,"9e0b33dc-0449-4d7b-81d1-819911022c4b"),sQuery(id+"F0.wireOp",EDGE,"4d3532ee-43e3-4ca5-8400-a337cc55de55"),sQuery(id+"F0.wireOp",EDGE,"b9521aba-0c13-404d-9ce5-fb4589b62adf"),sQuery(id+"F0.wireOp",EDGE,"1149e1d0-5c81-482d-91ef-e560cf3edfd4"),sQuery(id+"F0.wireOp",EDGE,"0e398b80-a194-43b6-abc4-8786c8afef94.0"),sQuery(id+"F0.wireOp",EDGE,"5c6cbf64-2606-42f1-a4f5-0fc4a52ef3d7.0"),sQuery(id+"F0.wireOp",EDGE,"4d74fcce-4ab5-4bb6-ac6c-11029cad5eb7.trimOffspring"),sQuery(id+"F0.wireOp",EDGE,"da44d0a2-5c99-41ba-b335-9bb7506599a5.trimOffspring"),sQuery(id+"F0.wireOp",EDGE,"3b17bb44-121f-48b3-8c56-af9687b41b5b.trimOffspring"),sQuery(id+"F0.wireOp",EDGE,"9b0d49c6-0c42-47df-9a44-ddff2b38050b.trimOffspring"),sQuery(id+"F0.wireOp",EDGE,"8bf3d40e-4444-4454-950e-a382101168c0.trimOffspring"),sQuery(id+"F0.wireOp",EDGE,"E7"),sQuery(id+"F0.wireOp",EDGE,"E8"),sQuery(id+"F0.wireOp",EDGE,"E9"),sQuery(id+"F0.wireOp",EDGE,"E10.bottom"),sQuery(id+"F0.wireOp",EDGE,"E10.top"),sQuery(id+"F0.wireOp",EDGE,"E10.left"),sQuery(id+"F0.wireOp",EDGE,"E10.right"),sQuery(id+"F0.wireOp",EDGE,"E11"),sQuery(id+"F0.wireOp",EDGE,"E12"),sQuery(id+"F0.wireOp",EDGE,"E13"),sQuery(id+"F0.wireOp",EDGE,"E14.bottom"),sQuery(id+"F0.wireOp",EDGE,"E14.top"),sQuery(id+"F0.wireOp",EDGE,"E14.right"),sQuery(id+"F0.wireOp",EDGE,"E15.trimOffspring"),sQuery(id+"F0.wireOp",EDGE,"E16"),sQuery(id+"F0.wireOp",EDGE,"E17"),sQuery(id+"F0.wireOp",EDGE,"E18"),sQuery(id+"F0.wireOp",EDGE,"E19"),sQuery(id+"F0.wireOp",EDGE,"E20"),sQuery(id+"F0.wireOp",EDGE,"E21"),sQuery(id+"F0.wireOp",EDGE,"E22"),sQuery(id+"F0.wireOp",EDGE,"E23"),sQuery(id+"F0.wireOp",EDGE,"E24"),sQuery(id+"F0.wireOp",EDGE,"E25"),sQuery(id+"F0.wireOp",EDGE,"E26"),sQuery(id+"F0.wireOp",EDGE,"E27"),sQuery(id+"F0.wireOp",EDGE,"E28"),sQuery(id+"F0.wireOp",EDGE,"E29"),sQuery(id+"F0.wireOp",EDGE,"E30"),sQuery(id+"F0.wireOp",EDGE,"E31"),sQuery(id+"F0.wireOp",EDGE,"E32"),sQuery(id+"F0.wireOp",EDGE,"E33"),sQuery(id+"F0.wireOp",EDGE,"E34"),sQuery(id+"F0.wireOp",EDGE,"E35"),sQuery(id+"F0.wireOp",EDGE,"E36.trimOffspring"),sQuery(id+"F0.wireOp",EDGE,"E37.trimOffspring"),sQuery(id+"F0.wireOp",EDGE,"E38.trimOffspring"),sQuery(id+"F0.wireOp",EDGE,"E39.trimOffspring"),sQuery(id+"F0.wireOp",EDGE,"E40.trimOffspring"),sQuery(id+"F0.wireOp",EDGE,"E41.trimOffspring"),sQuery(id+"F0.wireOp",EDGE,"E42")])],"isStart":false});
            cPlane(context, id + "F14", {"entities" : qUnion([Q0, Q1]), "cplaneType" : CPlaneType.MID_PLANE, "offset" : 150 * mm, "width" : 150 * mm, "height" : 150 * mm});
        }
        {
            var Q0;
            Q0=qCreatedBy(id+"F14.planeOp",FACE);
            var sketch = newSketch(context, id + "F15", { "sketchPlane" : qUnion([Q0])});
            skLineSegment(sketch, "E184", {"start": v(-2.44, -30.46) * mm, "end": v(-62.44, -30.46) * mm});
            skArc(sketch, "E185", {"start": v(-62.44, -30.46) * mm, "mid": v(-32.44, -60.46) * mm, "end": v(-2.44, -30.46) * mm});
            skArc(sketch, "E186", {"start": v(-2.44, -30.46) * mm, "mid": v(-32.44, -0.5) * mm, "end": v(-62.44, -30.46) * mm, "construction": true});
            skSolve(sketch);
        }
        {
            var Q0;
            Q0 = qSketchRegion(id + "F15", true);
            var Q1;
            Q1=sQuery(id+"F15.wireOp",EDGE,"E184");
            revolve(context, id + "F16", {"entities" : qUnion([Q0]), "axis" : qUnion([Q1]), "revolveType" : RevolveType.FULL});
        }
        {
            var Q0;
            Q0=makeQuery(id+"F1.opExtrude","SWEPT_FACE",FACE,{"disambiguationData":[OSD([sQuery(id+"F0.wireOp",EDGE,"E44")])]});
            var sketch = newSketch(context, id + "F17", { "sketchPlane" : qUnion([Q0])});
            skLineSegment(sketch, "E187", {"start": v(-65, -207.06) * mm, "end": v(-65, -137.06) * mm});
            skLineSegment(sketch, "E188", {"start": v(-65, -137.06) * mm, "end": v(-65, -107.06) * mm});
            skLineSegment(sketch, "E189", {"start": v(-65, -107.06) * mm, "end": v(0, -107.06) * mm});
            skLineSegment(sketch, "E190", {"start": v(0, -107.06) * mm, "end": v(0, -137.06) * mm});
            skLineSegment(sketch, "E191", {"start": v(0, -137.06) * mm, "end": v(0, -207.06) * mm});
            skLineSegment(sketch, "E192", {"start": v(0, -207.06) * mm, "end": v(-65, -207.06) * mm});
            skSolve(sketch);
        }
        {
            var Q0;
            Q0 = qSketchRegion(id + "F17", true);
            extrude(context, id + "F18", {"entities" : qUnion([Q0]), "oppositeDirection" : true, "depth" : 4 * mm});
        }
    });
